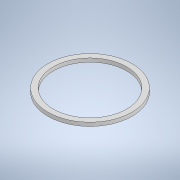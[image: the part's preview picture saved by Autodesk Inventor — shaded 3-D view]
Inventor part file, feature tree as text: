
AUTODESK INVENTOR PART (.ipt)
format: ipt  version: 2020 (Build 240168000, 168)  size: 104,448 bytes
history: native  units: mm
features: revolve x1, sketch x1
ambient origin geometry x8: Origin, YZ Plane, XZ Plane, XY Plane, X Axis, Y Axis, Z Axis, Center Point
bodies: Solid1 (feature_tree)
feature tree (2):
  revolve  "Revolution1"  [1 undecoded]
  sketch  "Sketch2"  dims[d4=90.0deg]
note: 1 required parameter value undecoded (feature->parameter linkage not recoverable at this tier; creation-order binding heuristic only, values carry confidence <= 0.55)
